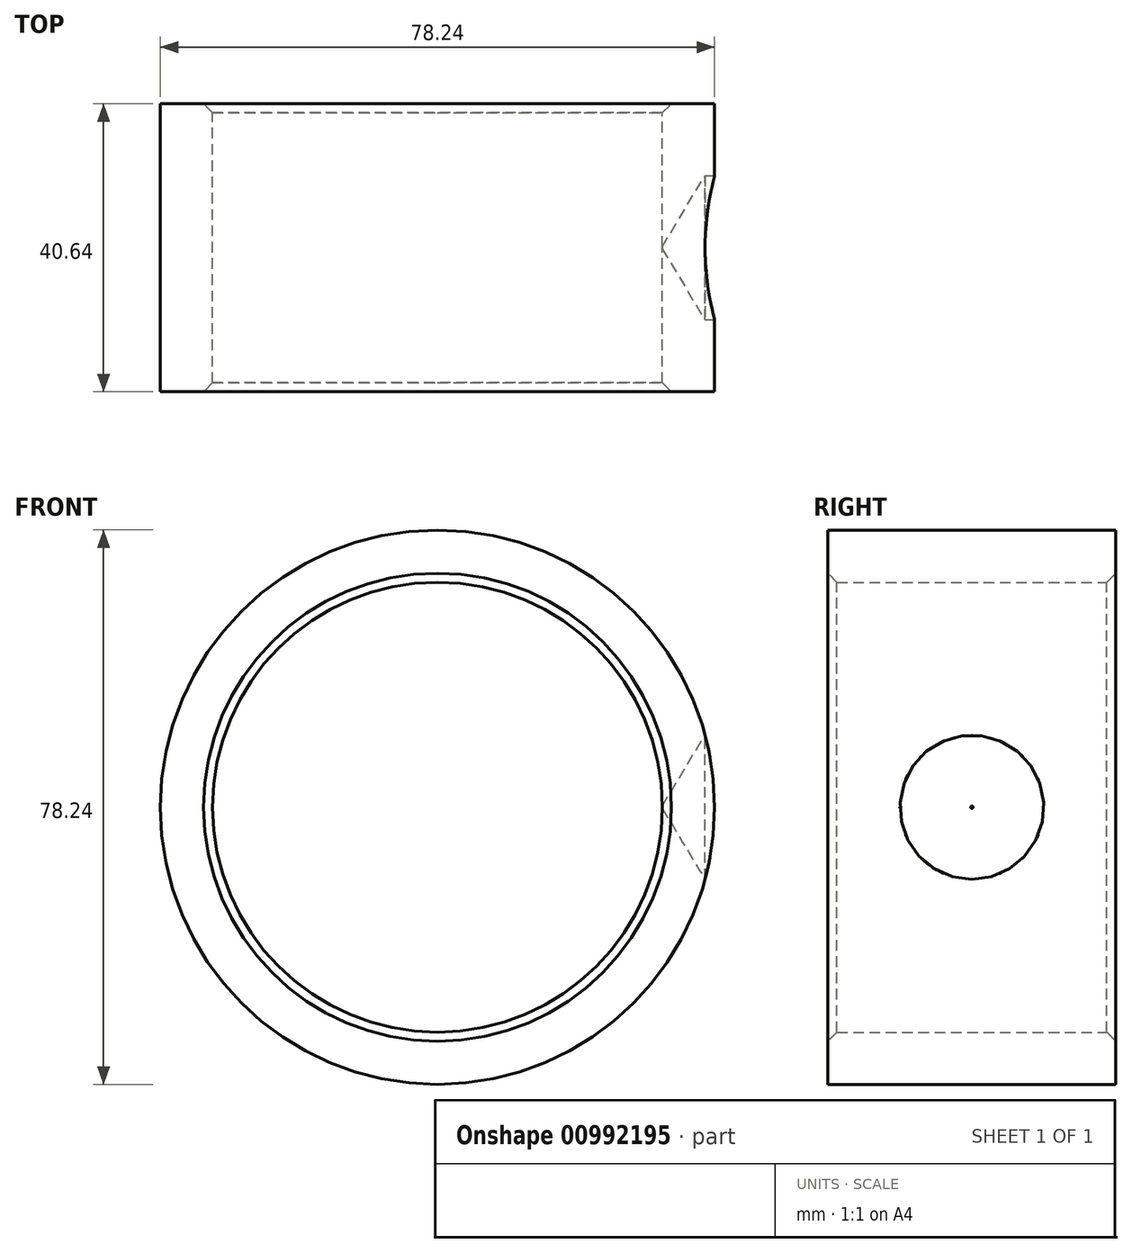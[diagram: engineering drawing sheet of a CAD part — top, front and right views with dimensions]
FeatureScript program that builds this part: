
annotation { "Feature Type Name" : "Feature", "Feature Type Description" : "" }
export const myFeature = defineFeature(function(context is Context, id is Id, definition is map)
    precondition{}
    {
        {
            var Q0;
            Q0=qCreatedBy(makeId("Front.planeOp"),FACE);
            var sketch = newSketch(context, id + "F0", { "sketchPlane" : qUnion([Q0])});
            skCircle(sketch, "E0", {"center": v(0, 0) * mm, "radius": 39.12 * mm});
            skCircle(sketch, "E1", {"center": v(0, 0) * mm, "radius": 31.75 * mm});
            skSolve(sketch);
        }
        {
            var Q0;
            Q0=makeQuery(id+"F0.imprint","IMPRINT",FACE,{"disambiguationData":[TD([[makeQuery(id+"F0.imprint","IMPRINT",EDGE,{"derivedFrom":sQuery(id+"F0.wireOp",EDGE,"E0")}),1.0]])]});
            extrude(context, id + "F1", {"entities" : qUnion([Q0]), "depth" : 40.64 * mm, "offsetDistance" : 25.4 * mm});
        }
        {
            var Q0;
            Q0=makeQuery(id+"F1.opExtrude","CAP_EDGE",EDGE,{"disambiguationData":[OSD([sQuery(id+"F0.wireOp",EDGE,"E1")])],"isStart":false});
            var Q1;
            Q1=makeQuery(id+"F1.opExtrude","CAP_EDGE",EDGE,{"disambiguationData":[OSD([sQuery(id+"F0.wireOp",EDGE,"E1")])],"isStart":true});
            chamfer(context, id + "F2", {"entities" : qUnion([Q0, Q1]), "width" : 1.27 * mm, "tangentPropagation" : true});
        }
        {
            var Q0;
            Q0=qCreatedBy(makeId("Right.planeOp"),FACE);
            cPlane(context, id + "F3", {"entities" : qUnion([Q0]), "cplaneType" : CPlaneType.OFFSET, "offset" : 39.12 * mm, "width" : 152.4 * mm, "height" : 152.4 * mm});
        }
        {
            var Q0;
            Q0=qCreatedBy(id+"F3.planeOp",FACE);
            var sketch = newSketch(context, id + "F4", { "sketchPlane" : qUnion([Q0])});
            skPoint(sketch, "E2", {"position": v(0, 0) * mm});
            skPoint(sketch, "E3", {"position": v(-20.32, 0) * mm});
            skSolve(sketch);
        }
        {
            var Q0;
            Q0=sQuery(id+"F4.wireOp",VERTEX,"E3");
            var Q1;
            Q1=makeQuery(id+"F1.opExtrude","SWEPT_BODY",BODY,{"disambiguationData":[OSD([sQuery(id+"F0.wireOp",EDGE,"E0"),sQuery(id+"F0.wireOp",EDGE,"E1")])]});
            hole(context, id + "F5", {"style" : HoleStyle.SIMPLE, "endStyle" : HoleEndStyle.BLIND, "holeDiameter" : 20.32 * mm, "majorDiameter" : 6.35 * mm, "holeDepth" : 0.03 * mm, "isTappedThrough" : true, "tappedDepth" : 12.7 * mm, "tapClearance" : 3, "locations" : qUnion([Q0]), "scope" : qUnion([Q1])});
        }
    });
